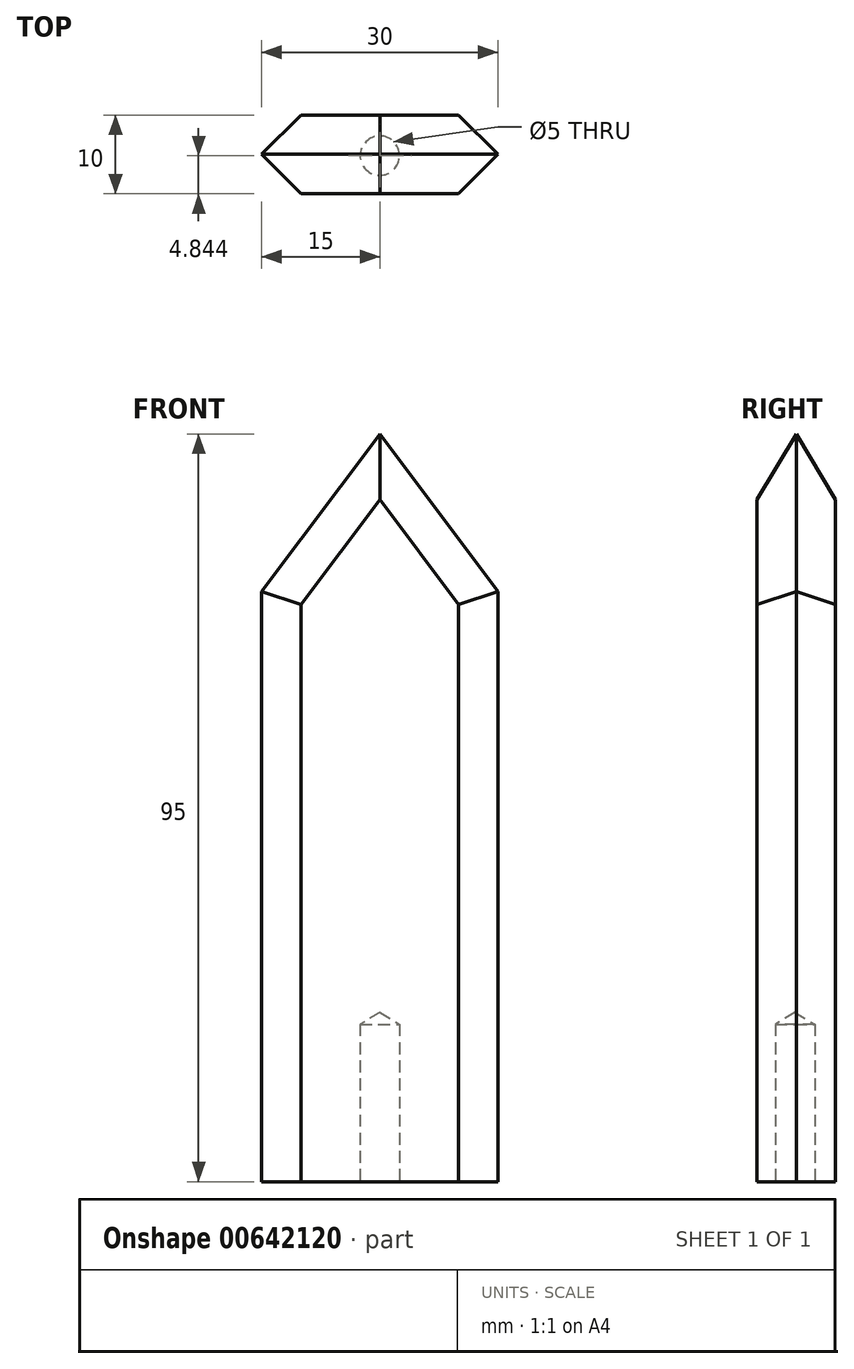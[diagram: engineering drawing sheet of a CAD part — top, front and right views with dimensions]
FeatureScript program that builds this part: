
annotation { "Feature Type Name" : "Feature", "Feature Type Description" : "" }
export const myFeature = defineFeature(function(context is Context, id is Id, definition is map)
    precondition{}
    {
        {
            var Q0;
            Q0=qCreatedBy(makeId("Front.planeOp"),FACE);
            var sketch = newSketch(context, id + "F0", { "sketchPlane" : qUnion([Q0])});
            skLineSegment(sketch, "E0", {"start": v(-15, 40.13) * mm, "end": v(-15, -34.87) * mm});
            skLineSegment(sketch, "E1", {"start": v(15, 40.13) * mm, "end": v(15, -34.87) * mm});
            skLineSegment(sketch, "E2", {"start": v(-15, 40.13) * mm, "end": v(0, 60.13) * mm});
            skLineSegment(sketch, "E3", {"start": v(0, 60.13) * mm, "end": v(15, 40.13) * mm});
            skLineSegment(sketch, "E4", {"start": v(-15, -34.87) * mm, "end": v(15, -34.87) * mm});
            skSolve(sketch);
        }
        {
            var Q0;
            Q0=makeQuery(id+"F0.imprint","IMPRINT",FACE,{"disambiguationData":[TD([[makeQuery(id+"F0.imprint","IMPRINT",EDGE,{"derivedFrom":sQuery(id+"F0.wireOp",EDGE,"E0")}),1.0]])]});
            extrude(context, id + "F1", {"entities" : qUnion([Q0]), "depth" : 10 * mm, "offsetDistance" : 25 * mm});
        }
        {
            var Q0;
            Q0=makeQuery(id+"F1.opExtrude","CAP_EDGE",EDGE,{"disambiguationData":[OSD([sQuery(id+"F0.wireOp",EDGE,"E0")])],"isStart":false});
            var Q1;
            Q1=makeQuery(id+"F1.opExtrude","CAP_EDGE",EDGE,{"disambiguationData":[OSD([sQuery(id+"F0.wireOp",EDGE,"E0")])],"isStart":true});
            var Q2;
            Q2=makeQuery(id+"F1.opExtrude","CAP_EDGE",EDGE,{"disambiguationData":[OSD([sQuery(id+"F0.wireOp",EDGE,"E2")])],"isStart":false});
            var Q3;
            Q3=makeQuery(id+"F1.opExtrude","CAP_EDGE",EDGE,{"disambiguationData":[OSD([sQuery(id+"F0.wireOp",EDGE,"E2")])],"isStart":true});
            var Q4;
            Q4=makeQuery(id+"F1.opExtrude","CAP_EDGE",EDGE,{"disambiguationData":[OSD([sQuery(id+"F0.wireOp",EDGE,"E3")])],"isStart":false});
            var Q5;
            Q5=makeQuery(id+"F1.opExtrude","CAP_EDGE",EDGE,{"disambiguationData":[OSD([sQuery(id+"F0.wireOp",EDGE,"E3")])],"isStart":true});
            var Q6;
            Q6=makeQuery(id+"F1.opExtrude","CAP_EDGE",EDGE,{"disambiguationData":[OSD([sQuery(id+"F0.wireOp",EDGE,"E1")])],"isStart":false});
            var Q7;
            Q7=makeQuery(id+"F1.opExtrude","CAP_EDGE",EDGE,{"disambiguationData":[OSD([sQuery(id+"F0.wireOp",EDGE,"E1")])],"isStart":true});
            chamfer(context, id + "F2", {"entities" : qUnion([Q0, Q1, Q2, Q3, Q4, Q5, Q6, Q7]), "width" : 5 * mm, "tangentPropagation" : true});
        }
        {
            var Q0;
            Q0=makeQuery(id+"F1.opExtrude","SWEPT_FACE",FACE,{"disambiguationData":[OSD([sQuery(id+"F0.wireOp",EDGE,"E4")])]});
            var sketch = newSketch(context, id + "F3", { "sketchPlane" : qUnion([Q0])});
            skCircle(sketch, "E5", {"center": v(0, 5.16) * mm, "radius": 2.51 * mm});
            skSolve(sketch);
        }
        {
            var Q0;
            Q0=sQuery(id+"F3.wireOp",VERTEX,"E5.center");
            var Q1;
            Q1=makeQuery(id+"F1.opExtrude","SWEPT_BODY",BODY,{"disambiguationData":[OSD([sQuery(id+"F0.wireOp",EDGE,"E0"),sQuery(id+"F0.wireOp",EDGE,"E1"),sQuery(id+"F0.wireOp",EDGE,"E2"),sQuery(id+"F0.wireOp",EDGE,"E3"),sQuery(id+"F0.wireOp",EDGE,"E4")])]});
            hole(context, id + "F4", {"style" : HoleStyle.SIMPLE, "endStyle" : HoleEndStyle.BLIND, "holeDiameter" : 5 * mm, "majorDiameter" : 5 * mm, "holeDepth" : 20 * mm, "isTappedThrough" : true, "tappedDepth" : 12 * mm, "tapClearance" : 3, "locations" : qUnion([Q0]), "scope" : qUnion([Q1])});
        }
    });
